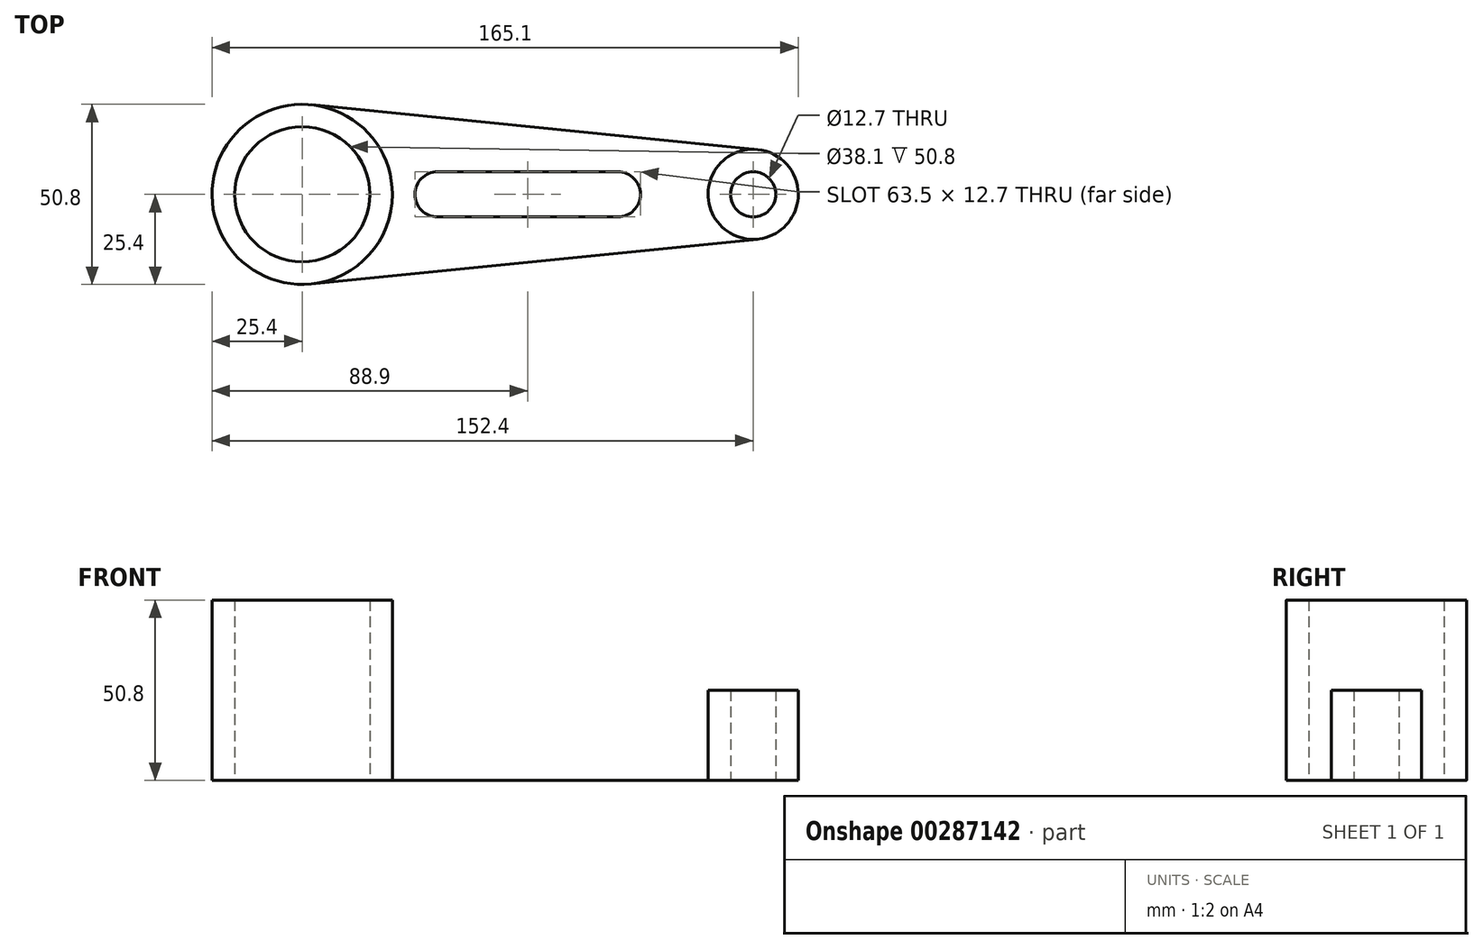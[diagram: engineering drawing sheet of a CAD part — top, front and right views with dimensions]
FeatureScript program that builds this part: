
annotation { "Feature Type Name" : "Feature", "Feature Type Description" : "" }
export const myFeature = defineFeature(function(context is Context, id is Id, definition is map)
    precondition{}
    {
        {
            var Q0;
            Q0=qCreatedBy(makeId("Top.planeOp"),FACE);
            var sketch = newSketch(context, id + "F0", { "sketchPlane" : qUnion([Q0])});
            skCircle(sketch, "E0", {"center": v(0, 0) * mm, "radius": 19.05 * mm});
            skCircle(sketch, "E1", {"center": v(0, 0) * mm, "radius": 25.4 * mm});
            skLineSegment(sketch, "E2", {"start": v(0, 0) * mm, "end": v(38.1, 0) * mm});
            skCircle(sketch, "E3", {"center": v(127, 0) * mm, "radius": 6.35 * mm});
            skCircle(sketch, "E4", {"center": v(127, 0) * mm, "radius": 12.7 * mm});
            skLineSegment(sketch, "E5", {"start": v(38.1, 0) * mm, "end": v(88.9, 0) * mm});
            skLineSegment(sketch, "E6", {"start": v(88.9, 0) * mm, "end": v(127, 0) * mm});
            skLineSegment(sketch, "E7", {"start": v(38.1, 0) * mm, "end": v(38.1, 6.35) * mm});
            skLineSegment(sketch, "E8", {"start": v(38.1, 0) * mm, "end": v(38.1, -6.35) * mm});
            skLineSegment(sketch, "E9", {"start": v(88.9, 0) * mm, "end": v(88.9, 6.35) * mm});
            skLineSegment(sketch, "E10", {"start": v(88.9, 0) * mm, "end": v(88.9, -6.35) * mm});
            skLineSegment(sketch, "E11", {"start": v(38.1, -6.35) * mm, "end": v(88.9, -6.35) * mm});
            skLineSegment(sketch, "E12", {"start": v(38.1, 6.35) * mm, "end": v(88.9, 6.35) * mm});
            skArc(sketch, "E13", {"start": v(38.1, -6.35) * mm, "mid": v(31.75, 0) * mm, "end": v(38.1, 6.35) * mm});
            skArc(sketch, "E14", {"start": v(88.9, 6.35) * mm, "mid": v(95.25, 0) * mm, "end": v(88.9, -6.35) * mm});
            skLineSegment(sketch, "E15", {"start": v(2.54, 25.27) * mm, "end": v(128.27, 12.64) * mm});
            skLineSegment(sketch, "E16", {"start": v(2.54, -25.27) * mm, "end": v(128.27, -12.64) * mm});
            skSolve(sketch);
        }
        {
            var Q0;
            {var subQ9=sQuery(id+"F0.wireOp",EDGE,"E12");Q0=makeQuery(id+"F0.imprint","IMPRINT",FACE,{"disambiguationData":[TD([[makeQuery(id+"F0.imprint","IMPRINT",EDGE,{"derivedFrom":subQ9}),1.0]])]});}
            var Q1;
            {var subQ11=sQuery(id+"F0.wireOp",EDGE,"E11");Q1=makeQuery(id+"F0.imprint","IMPRINT",FACE,{"disambiguationData":[TD([[makeQuery(id+"F0.imprint","IMPRINT",EDGE,{"derivedFrom":subQ11}),-1.0]])]});}
            extrude(context, id + "F1", {"entities" : qUnion([Q0, Q1]), "depth" : 1 / 101.6 * mm});
        }
        {
            var Q0;
            Q0=makeQuery(id+"F0.imprint","IMPRINT",FACE,{"disambiguationData":[TD([[makeQuery(id+"F0.imprint","IMPRINT",EDGE,{"derivedFrom":sQuery(id+"F0.wireOp",EDGE,"E3")}),-1.0]])]});
            extrude(context, id + "F2", {"entities" : qUnion([Q0]), "operationType" : NewBodyOperationType.ADD, "depth" : 25.4 * mm});
        }
        {
            var Q0;
            Q0=makeQuery(id+"F0.imprint","IMPRINT",FACE,{"disambiguationData":[TD([[makeQuery(id+"F0.imprint","IMPRINT",EDGE,{"derivedFrom":sQuery(id+"F0.wireOp",EDGE,"E0")}),-1.0]])]});
            extrude(context, id + "F3", {"entities" : qUnion([Q0]), "operationType" : NewBodyOperationType.ADD, "depth" : 50.8 * mm});
        }
    });
